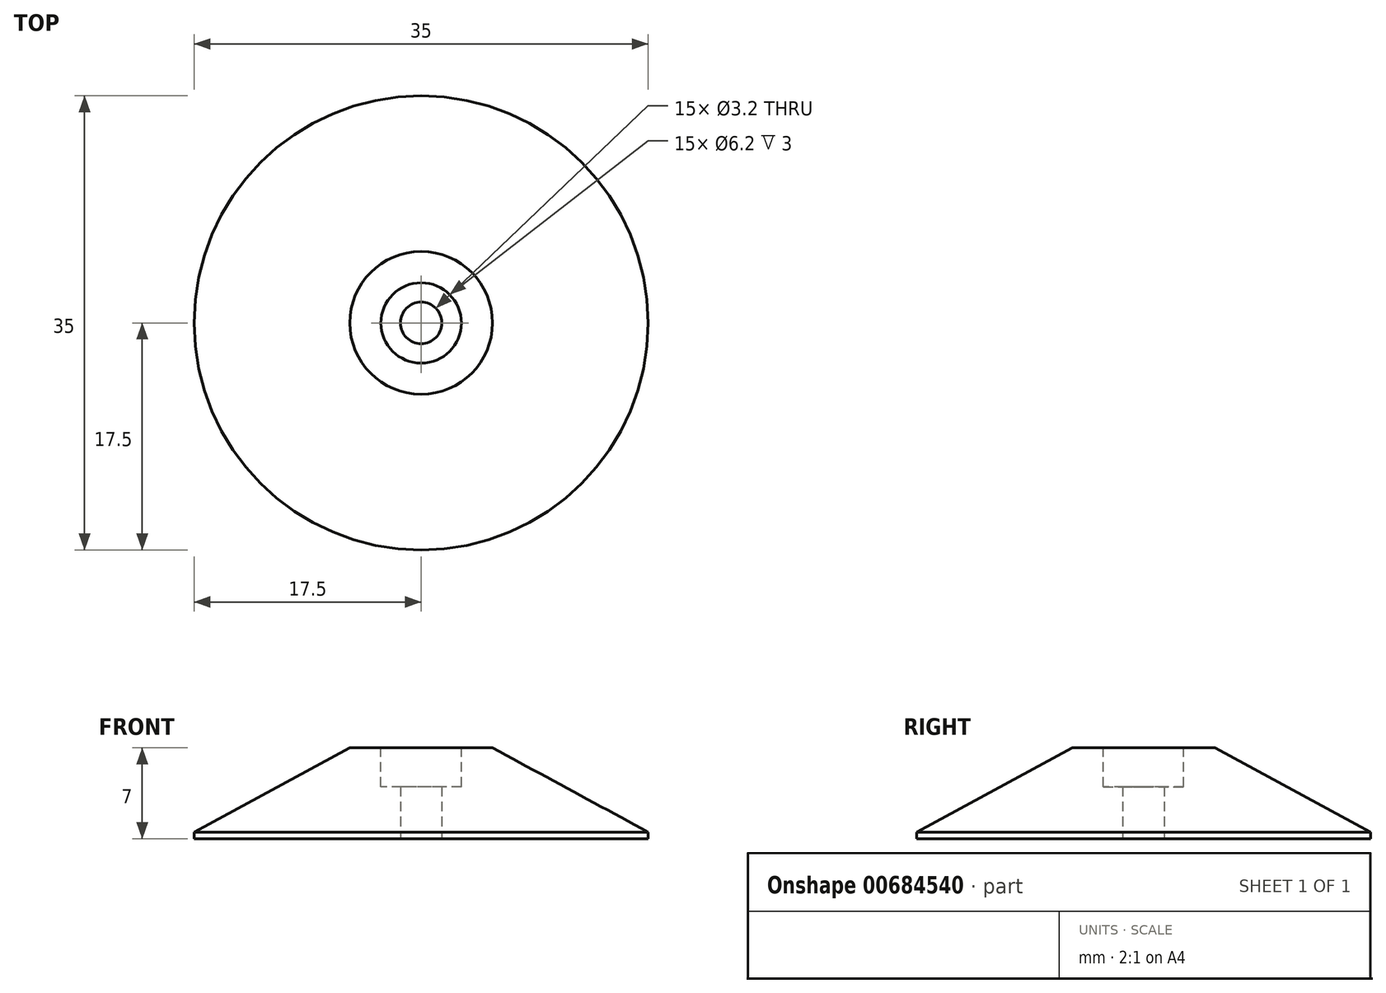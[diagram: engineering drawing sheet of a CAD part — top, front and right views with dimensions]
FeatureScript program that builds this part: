
annotation { "Feature Type Name" : "Feature", "Feature Type Description" : "" }
export const myFeature = defineFeature(function(context is Context, id is Id, definition is map)
    precondition{}
    {
        {
            var Q0;
            Q0=qCreatedBy(makeId("Top.planeOp"),FACE);
            var sketch = newSketch(context, id + "F0", { "sketchPlane" : qUnion([Q0])});
            skCircle(sketch, "E0", {"center": v(0, 0) * mm, "radius": 17.5 * mm});
            skCircle(sketch, "E1", {"center": v(0, 0) * mm, "radius": 1.6 * mm});
            skSolve(sketch);
        }
        {
            var Q0;
            Q0=makeQuery(id+"F0.imprint","IMPRINT",FACE,{"disambiguationData":[TD([[makeQuery(id+"F0.imprint","IMPRINT",EDGE,{"derivedFrom":sQuery(id+"F0.wireOp",EDGE,"E0")}),1.0]])]});
            extrude(context, id + "F1", {"entities" : qUnion([Q0]), "depth" : 7 * mm, "offsetDistance" : 25 * mm});
        }
        {
            var Q0;
            Q0=makeQuery(id+"F1.opExtrude","CAP_FACE",FACE,{"disambiguationData":[OSD([sQuery(id+"F0.wireOp",EDGE,"E0"),sQuery(id+"F0.wireOp",EDGE,"E1")])],"isStart":false});
            var sketch = newSketch(context, id + "F2", { "sketchPlane" : qUnion([Q0])});
            skCircle(sketch, "E2", {"center": v(0, 0) * mm, "radius": 3.1 * mm});
            skSolve(sketch);
        }
        {
            var Q0;
            Q0=makeQuery(id+"F2.imprint","IMPRINT",FACE,{"disambiguationData":[TD([[makeQuery(id+"F2.imprint","IMPRINT",EDGE,{"derivedFrom":sQuery(id+"F2.wireOp",EDGE,"E2")}),1.0]])]});
            extrude(context, id + "F3", {"entities" : qUnion([Q0]), "operationType" : NewBodyOperationType.REMOVE, "oppositeDirection" : true, "depth" : 3 * mm, "offsetDistance" : 25 * mm});
        }
        {
            var Q0;
            Q0=makeQuery(id+"F1.opExtrude","CAP_EDGE",EDGE,{"disambiguationData":[OSD([sQuery(id+"F0.wireOp",EDGE,"E0")])],"isStart":false});
            chamfer(context, id + "F4", {"entities" : qUnion([Q0]), "chamferType" : ChamferType.TWO_OFFSETS, "width1" : 12 * mm, "oppositeDirection" : false, "width2" : 6.5 * mm, "tangentPropagation" : true});
        }
    });
